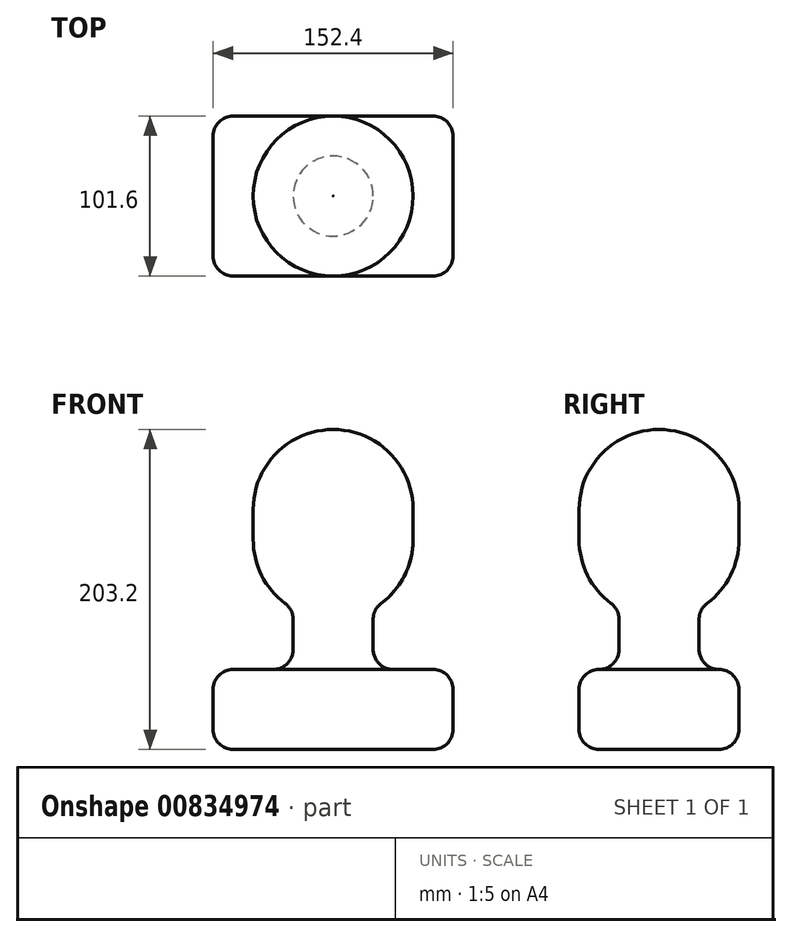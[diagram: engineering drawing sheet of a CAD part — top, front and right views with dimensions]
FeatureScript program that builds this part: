
annotation { "Feature Type Name" : "Feature", "Feature Type Description" : "" }
export const myFeature = defineFeature(function(context is Context, id is Id, definition is map)
    precondition{}
    {
        {
            var Q0;
            Q0=qCreatedBy(makeId("Top.planeOp"),FACE);
            var sketch = newSketch(context, id + "F0", { "sketchPlane" : qUnion([Q0])});
            skLineSegment(sketch, "E0.bottom", {"start": v(-76.2, 50.8) * mm, "end": v(76.2, 50.8) * mm});
            skLineSegment(sketch, "E0.top", {"start": v(-76.2, -50.8) * mm, "end": v(76.2, -50.8) * mm});
            skLineSegment(sketch, "E0.left", {"start": v(-76.2, 50.8) * mm, "end": v(-76.2, -50.8) * mm});
            skLineSegment(sketch, "E0.right", {"start": v(76.2, 50.8) * mm, "end": v(76.2, -50.8) * mm});
            skPoint(sketch, "E0.middle", {"position": v(0, 0) * mm});
            skSolve(sketch);
        }
        {
            var Q0;
            Q0=makeQuery(id+"F0.imprint","IMPRINT",FACE,{"disambiguationData":[TD([[makeQuery(id+"F0.imprint","IMPRINT",EDGE,{"derivedFrom":sQuery(id+"F0.wireOp",EDGE,"E0.bottom")}),-1.0]])]});
            extrude(context, id + "F1", {"entities" : qUnion([Q0]), "oppositeDirection" : true, "depth" : 50.8 * mm, "offsetDistance" : 25.4 * mm});
        }
        {
            var Q0;
            Q0=qCreatedBy(makeId("Front.planeOp"),FACE);
            var sketch = newSketch(context, id + "F2", { "sketchPlane" : qUnion([Q0])});
            skLineSegment(sketch, "E1", {"start": v(0, 0) * mm, "end": v(0, 152.4) * mm});
            skLineSegment(sketch, "E2", {"start": v(25.4, 38.56) * mm, "end": v(25.4, 0) * mm});
            skLineSegment(sketch, "E3", {"start": v(25.4, 0) * mm, "end": v(0, 0) * mm});
            skLineSegment(sketch, "E4", {"start": v(0, 101.6) * mm, "end": v(50.8, 101.6) * mm});
            skArc(sketch, "E5.trimOffspring", {"start": v(50.8, 101.6) * mm, "mid": v(35.92, 137.52) * mm, "end": v(0, 152.4) * mm});
            skLineSegment(sketch, "E6", {"start": v(50.8, 101.6) * mm, "end": v(50.8, 82.55) * mm});
            skLineSegment(sketch, "E7", {"start": v(50.8, 82.55) * mm, "end": v(0, 82.55) * mm});
            skArc(sketch, "E8", {"start": v(0, 31.75) * mm, "mid": v(35.92, 46.63) * mm, "end": v(50.8, 82.55) * mm});
            skSolve(sketch);
        }
        {
            var Q0;
            {var subQ4=sQuery(id+"F2.wireOp",EDGE,"E2");Q0=makeQuery(id+"F2.imprint","IMPRINT",FACE,{"disambiguationData":[TD([[makeQuery(id+"F2.imprint","IMPRINT",EDGE,{"derivedFrom":subQ4}),-1.0]])]});}
            var Q1;
            {var subQ0=sQuery(id+"F2.wireOp",EDGE,"Vdrke3j5-S48I-vTwe-A0sj-LHQhQxHpboUg");var subQ1=sQuery(id+"F2.wireOp",EDGE,"E1");var subQ2=makeQuery(id+"F2.imprint","INTERSECT",VERTEX,{"disambiguationData":[OD(0.0)],"derivedFrom":[subQ1,subQ0]});Q1=makeQuery(id+"F2.imprint","IMPRINT",FACE,{"disambiguationData":[TD([[makeQuery(id+"F2.imprint","IMPRINT",EDGE,{"disambiguationData":[TD([[subQ2,1.0]])],"derivedFrom":subQ1}),-1.0]])]});}
            var Q2;
            {var subQ0=sQuery(id+"F2.wireOp",EDGE,"E4");Q2=makeQuery(id+"F2.imprint","IMPRINT",FACE,{"disambiguationData":[TD([[makeQuery(id+"F2.imprint","IMPRINT",EDGE,{"derivedFrom":subQ0}),-1.0]])]});}
            var Q3;
            {var subQ0=sQuery(id+"F2.wireOp",EDGE,"E7");Q3=makeQuery(id+"F2.imprint","IMPRINT",FACE,{"disambiguationData":[TD([[makeQuery(id+"F2.imprint","IMPRINT",EDGE,{"derivedFrom":subQ0}),1.0]])]});}
            var Q4;
            Q4=sQuery(id+"F2.wireOp",EDGE,"E1");
            revolve(context, id + "F3", {"operationType" : NewBodyOperationType.ADD, "surfaceOperationType" : NewSurfaceOperationType.NEW, "entities" : qUnion([Q0, Q1, Q2, Q3]), "axis" : qUnion([Q4]), "revolveType" : RevolveType.FULL});
        }
        {
            var Q0;
            Q0=makeQuery(id+"F1.opExtrude","CAP_FACE",FACE,{"disambiguationData":[OSD([sQuery(id+"F0.wireOp",EDGE,"E0.bottom"),sQuery(id+"F0.wireOp",EDGE,"E0.top"),sQuery(id+"F0.wireOp",EDGE,"E0.left"),sQuery(id+"F0.wireOp",EDGE,"E0.right")])],"isStart":true});
            var Q1;
            Q1=makeQuery(id+"F1.opExtrude","SWEPT_FACE",FACE,{"disambiguationData":[OSD([sQuery(id+"F0.wireOp",EDGE,"E0.top")])]});
            var Q2;
            Q2=makeQuery(id+"F1.opExtrude","SWEPT_FACE",FACE,{"disambiguationData":[OSD([sQuery(id+"F0.wireOp",EDGE,"E0.left")])]});
            var Q3;
            Q3=makeQuery(id+"F1.opExtrude","SWEPT_FACE",FACE,{"disambiguationData":[OSD([sQuery(id+"F0.wireOp",EDGE,"E0.bottom")])]});
            var Q4;
            Q4=makeQuery(id+"F1.opExtrude","SWEPT_FACE",FACE,{"disambiguationData":[OSD([sQuery(id+"F0.wireOp",EDGE,"E0.right")])]});
            var Q5;
            Q5=makeQuery(id+"F1.opExtrude","CAP_FACE",FACE,{"disambiguationData":[OSD([sQuery(id+"F0.wireOp",EDGE,"E0.bottom"),sQuery(id+"F0.wireOp",EDGE,"E0.top"),sQuery(id+"F0.wireOp",EDGE,"E0.left"),sQuery(id+"F0.wireOp",EDGE,"E0.right")])],"isStart":false});
            var Q6;
            Q6=makeQuery(id+"F3.opRevolve","SWEPT_FACE",FACE,{"disambiguationData":[OSD([sQuery(id+"F2.wireOp",EDGE,"E2")])]});
            fillet(context, id + "F4", {"entities" : qUnion([Q0, Q1, Q2, Q3, Q4, Q5, Q6]), "radius" : 12.7 * mm, "tangentPropagation" : true, "allowEdgeOverflow" : false});
        }
    });
